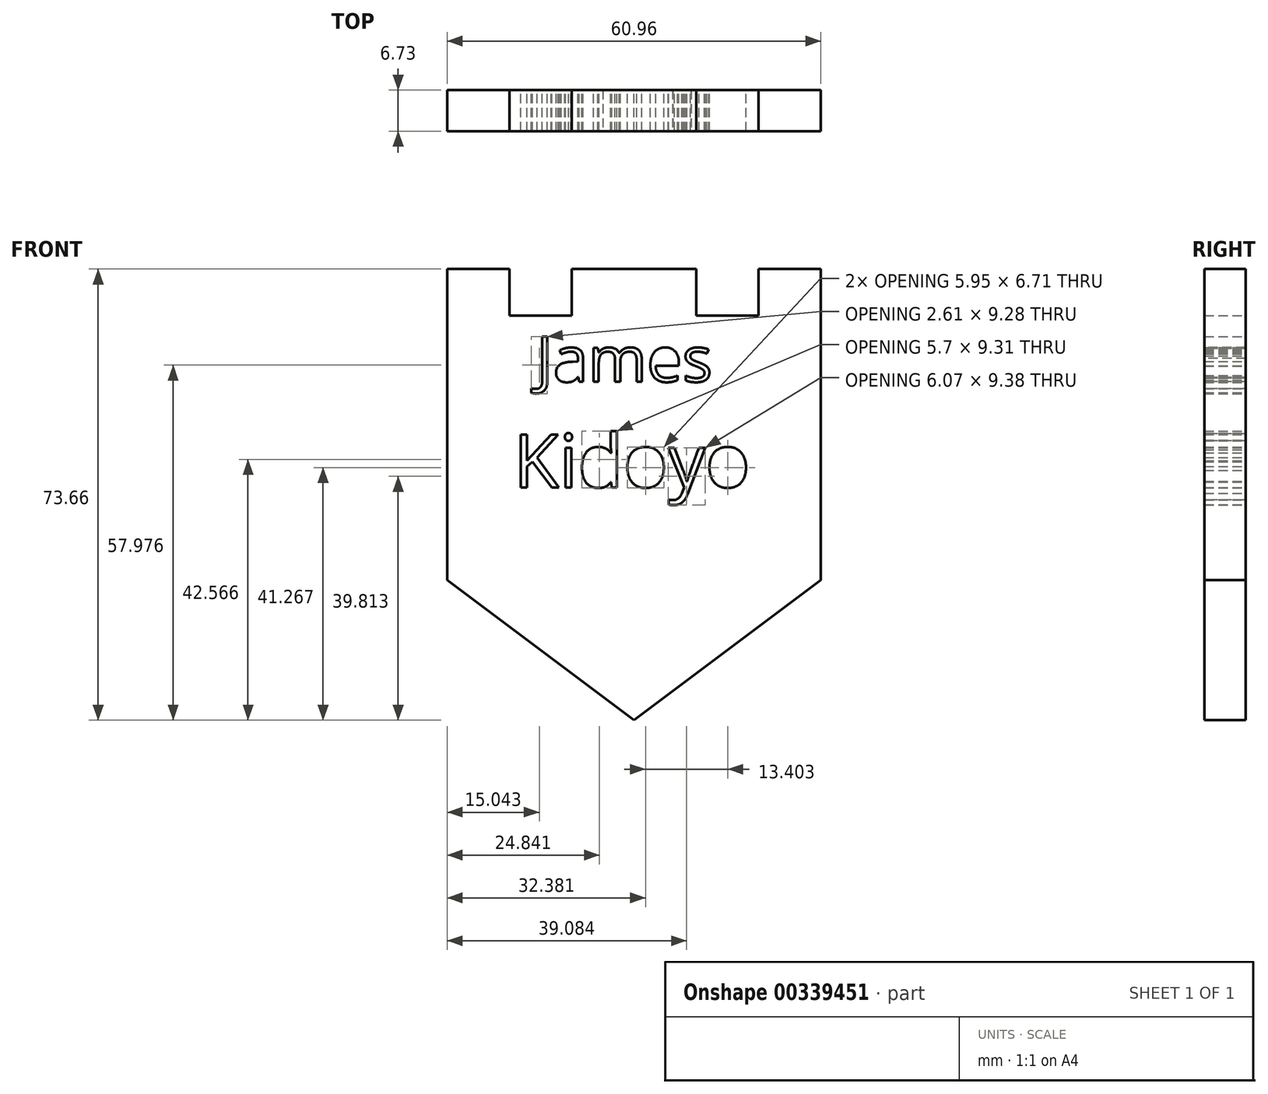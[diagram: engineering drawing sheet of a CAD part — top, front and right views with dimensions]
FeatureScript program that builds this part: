
annotation { "Feature Type Name" : "Feature", "Feature Type Description" : "" }
export const myFeature = defineFeature(function(context is Context, id is Id, definition is map)
    precondition{}
    {
        {
            var Q0;
            Q0=qCreatedBy(makeId("Front.planeOp"),FACE);
            var sketch = newSketch(context, id + "F0", { "sketchPlane" : qUnion([Q0])});
            skLineSegment(sketch, "E0", {"start": v(0, 50.8) * mm, "end": v(-10.16, 50.8) * mm});
            skLineSegment(sketch, "E1", {"start": v(-10.16, 50.8) * mm, "end": v(-10.16, 43.18) * mm});
            skLineSegment(sketch, "E2", {"start": v(-10.16, 43.18) * mm, "end": v(-20.32, 43.18) * mm});
            skLineSegment(sketch, "E3", {"start": v(-20.32, 43.18) * mm, "end": v(-20.32, 50.8) * mm});
            skLineSegment(sketch, "E4", {"start": v(-20.32, 50.8) * mm, "end": v(-30.48, 50.8) * mm});
            skLineSegment(sketch, "E5", {"start": v(-30.48, 50.8) * mm, "end": v(-30.48, 0) * mm});
            skLineSegment(sketch, "E6", {"start": v(-30.48, 0) * mm, "end": v(0, -22.86) * mm});
            skLineSegment(sketch, "E7.MirrorCS", {"start": v(0, 50.8) * mm, "end": v(10.16, 50.8) * mm});
            skLineSegment(sketch, "E8.MirrorCS", {"start": v(10.16, 50.8) * mm, "end": v(10.16, 43.18) * mm});
            skLineSegment(sketch, "E9.MirrorCS", {"start": v(10.16, 43.18) * mm, "end": v(20.32, 43.18) * mm});
            skLineSegment(sketch, "E10.MirrorCS", {"start": v(20.32, 43.18) * mm, "end": v(20.32, 50.8) * mm});
            skLineSegment(sketch, "E11.MirrorCS", {"start": v(20.32, 50.8) * mm, "end": v(30.48, 50.8) * mm});
            skLineSegment(sketch, "E12.MirrorCS", {"start": v(30.48, 50.8) * mm, "end": v(30.48, 0) * mm});
            skLineSegment(sketch, "E13.MirrorCS", {"start": v(30.48, 0) * mm, "end": v(0, -22.86) * mm});
            skText(sketch, "E14", { "text": "James", "fontName": "OpenSans-Regular.ttf"});
            skText(sketch, "E15", { "text": "Kidoyo  ", "fontName": "OpenSans-Regular.ttf"});
            const initialGuessF0  = {"E14": [-0.01594, 0.03241, 1, 0, 0.00741], "E15": [-0.01965, 0.01517, 1, 0, 0.00871]};
            skSetInitialGuess(sketch, initialGuessF0);
            skSolve(sketch);
        }
        {
            var Q0;
            Q0=makeQuery(id+"F0.imprint","IMPRINT",FACE,{"disambiguationData":[TD([[makeQuery(id+"F0.imprint","IMPRINT",EDGE,{"derivedFrom":sQuery(id+"F0.wireOp",EDGE,"E0")}),1.0]])]});
            extrude(context, id + "F1", {"entities" : qUnion([Q0]), "depth" : 6.73 * mm});
        }
    });
